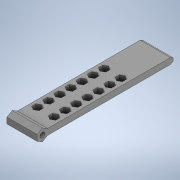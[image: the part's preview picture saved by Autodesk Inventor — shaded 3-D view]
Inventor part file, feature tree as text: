
AUTODESK INVENTOR PART (.ipt)
format: ipt  version: 2020 (Build 240168000, 168)  size: 300,544 bytes
history: native  units: in
note: dims shown in document units (in); Inventor stores cm internally (conversion verified against a paired STEP export)
features: sketch x4, extrude x3, plane x1, projected_geometry x1
ambient origin geometry x8: Origin, YZ Plane, XZ Plane, XY Plane, X Axis, Y Axis, Z Axis, Center Point
bodies: Solid1 (feature_tree)
feature tree (9):
  extrude  "Extrusion1"  Depth=3.5433in
  plane  "Work Plane1"
  extrude  "Extrusion2"  Depth=0.7874in
  extrude  "Extrusion3"  Depth=0.0787in
  sketch  "Sketch4"  dims[d6=0.7874in d7=0.0in d8=0.0787in d9=0.0787in d10=0.0787in d11=0.2273in d12=3.937in d14=0.2903in d15=0.3937in d17=0.3937in d19=3.937in d21=0.2903in d22=0.3937in d24=0.3937in d26=0.7874in d27=0.0in d28=3.2705in]
  sketch  "Sketch1"  dims[d0=0.1575in d1=3.5433in]
  sketch  "Sketch2"  dims[d2=0.1299in d3=0.7874in]
  sketch  "Sketch3"  dims[d4=0.0in d5=0.0787in]
  projected_geometry  "Projected Loop1"
